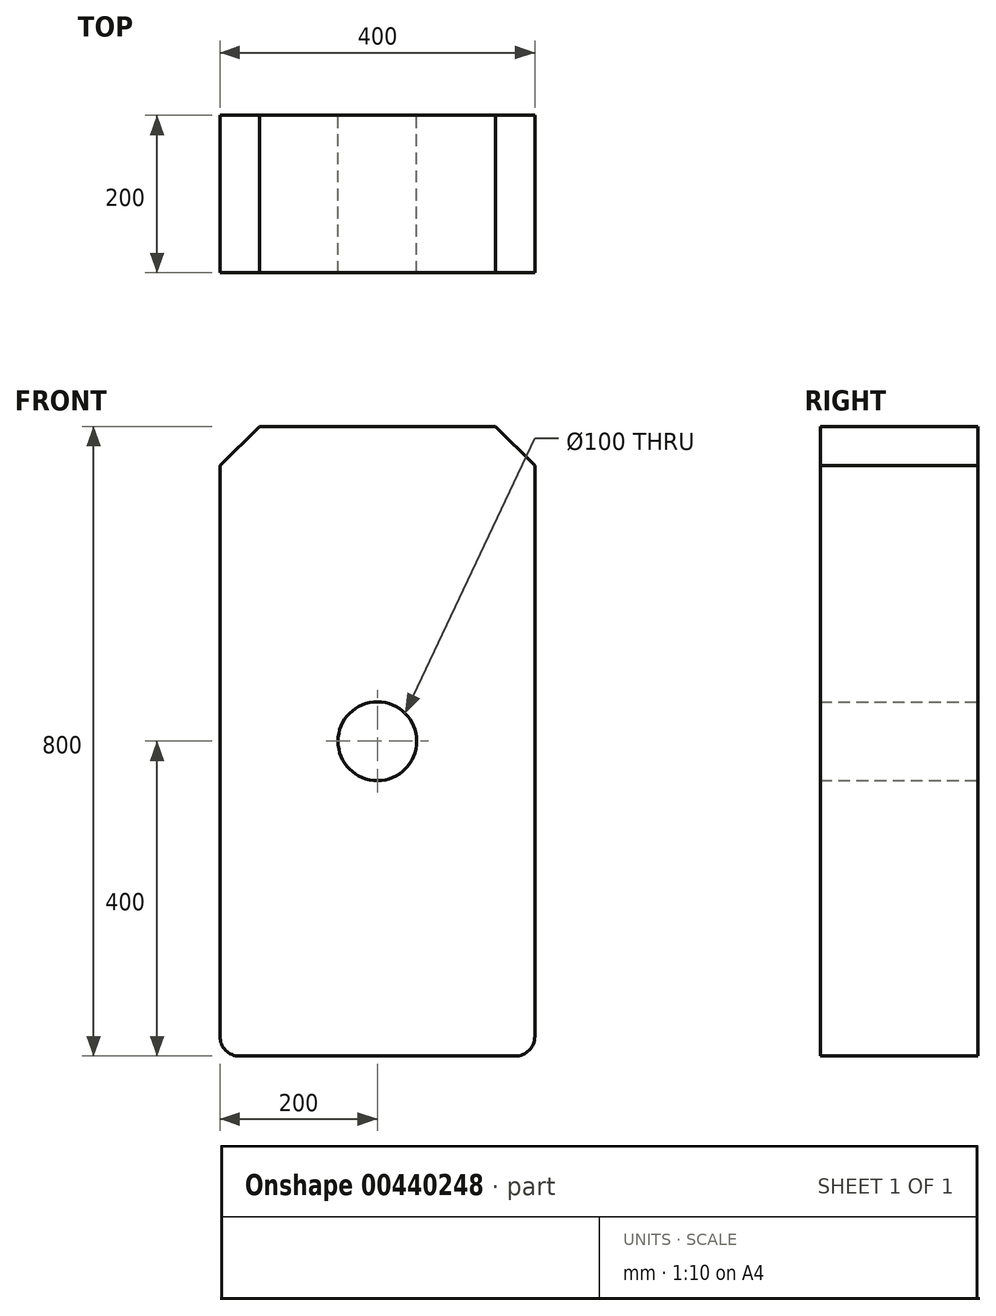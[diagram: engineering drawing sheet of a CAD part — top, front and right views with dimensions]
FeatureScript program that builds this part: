
annotation { "Feature Type Name" : "Feature", "Feature Type Description" : "" }
export const myFeature = defineFeature(function(context is Context, id is Id, definition is map)
    precondition{}
    {
        {
            var Q0;
            Q0=qCreatedBy(makeId("Front.planeOp"),FACE);
            var sketch = newSketch(context, id + "F0", { "sketchPlane" : qUnion([Q0])});
            skLineSegment(sketch, "E0.bottom", {"start": v(200, 400) * mm, "end": v(-200, 400) * mm});
            skLineSegment(sketch, "E0.top", {"start": v(175, -400) * mm, "end": v(-175, -400) * mm});
            skLineSegment(sketch, "E0.left", {"start": v(200, 400) * mm, "end": v(200, -375) * mm});
            skLineSegment(sketch, "E0.right", {"start": v(-200, 400) * mm, "end": v(-200, -375) * mm});
            skPoint(sketch, "E0.middle", {"position": v(0, 0) * mm});
            skPoint(sketch, "E1.visualSharp", {"position": v(-200, -400) * mm});
            skArc(sketch, "E1.filletArc", {"start": v(-200, -375) * mm, "mid": v(-192.68, -392.68) * mm, "end": v(-175, -400) * mm});
            skPoint(sketch, "E2.visualSharp", {"position": v(200, -400) * mm});
            skArc(sketch, "E2.filletArc", {"start": v(175, -400) * mm, "mid": v(192.68, -392.68) * mm, "end": v(200, -375) * mm});
            skSolve(sketch);
        }
        {
            var Q0;
            Q0 = qSketchRegion(id + "F0", true);
            extrude(context, id + "F1", {"entities" : qUnion([Q0]), "depth" : 200 * mm});
        }
        {
            var Q0;
            Q0=makeQuery(id+"F1.opExtrude","SWEPT_EDGE",EDGE,{"disambiguationData":[OSD([sQuery(id+"F0.wireOp",EDGE,"E0.bottom"),sQuery(id+"F0.wireOp",EDGE,"E0.left")])]});
            var Q1;
            Q1=makeQuery(id+"F1.opExtrude","SWEPT_EDGE",EDGE,{"disambiguationData":[OSD([sQuery(id+"F0.wireOp",EDGE,"E0.bottom"),sQuery(id+"F0.wireOp",EDGE,"E0.right")])]});
            chamfer(context, id + "F2", {"entities" : qUnion([Q0, Q1]), "width" : 50 * mm, "tangentPropagation" : true});
        }
        {
            var Q0;
            Q0=makeQuery(id+"F1.opExtrude","CAP_FACE",FACE,{"disambiguationData":[OSD([sQuery(id+"F0.wireOp",EDGE,"E0.bottom"),sQuery(id+"F0.wireOp",EDGE,"E0.top"),sQuery(id+"F0.wireOp",EDGE,"E0.left"),sQuery(id+"F0.wireOp",EDGE,"E0.right"),sQuery(id+"F0.wireOp",EDGE,"E1.filletArc"),sQuery(id+"F0.wireOp",EDGE,"E2.filletArc")])],"isStart":true});
            var sketch = newSketch(context, id + "F3", { "sketchPlane" : qUnion([Q0])});
            skCircle(sketch, "E3", {"center": v(0, 0) * mm, "radius": 50 * mm});
            skSolve(sketch);
        }
        {
            var Q0;
            Q0 = qSketchRegion(id + "F3", true);
            extrude(context, id + "F4", {"entities" : qUnion([Q0]), "operationType" : NewBodyOperationType.REMOVE, "endBound" : BoundingType.THROUGH_ALL, "oppositeDirection" : true, "depth" : 25.4 * mm});
        }
    });
